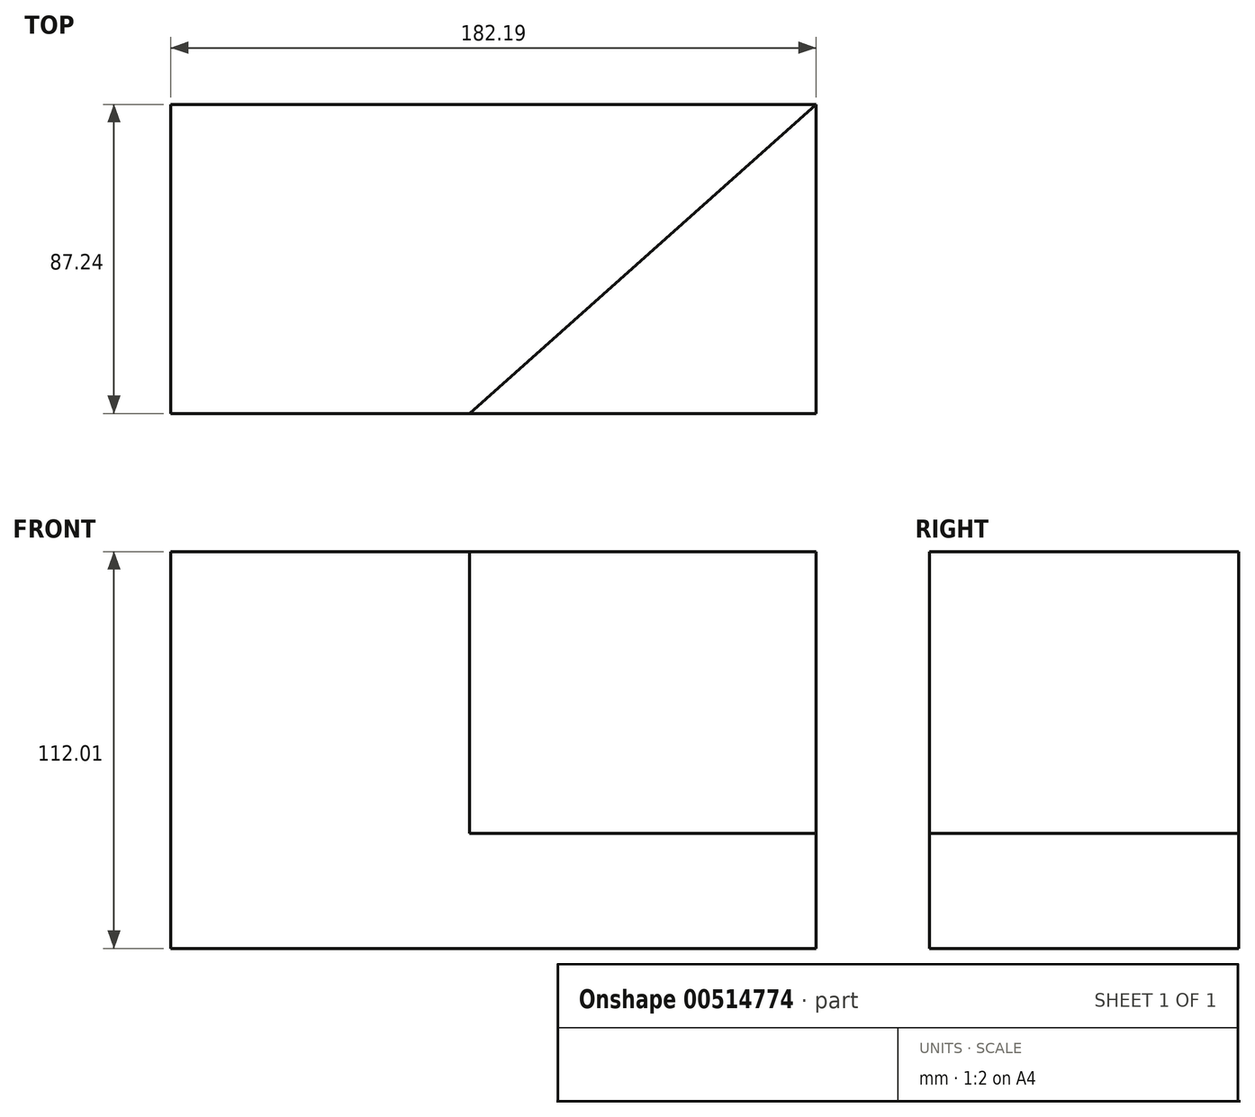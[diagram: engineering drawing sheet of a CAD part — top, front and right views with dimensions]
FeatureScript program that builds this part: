
annotation { "Feature Type Name" : "Feature", "Feature Type Description" : "" }
export const myFeature = defineFeature(function(context is Context, id is Id, definition is map)
    precondition{}
    {
        {
            var Q0;
            Q0=qCreatedBy(makeId("Top.planeOp"),FACE);
            var sketch = newSketch(context, id + "F0", { "sketchPlane" : qUnion([Q0])});
            skLineSegment(sketch, "E0.bottom", {"start": v(-84.35, 53.02) * mm, "end": v(97.84, 53.02) * mm});
            skLineSegment(sketch, "E0.top", {"start": v(-84.35, -34.22) * mm, "end": v(97.84, -34.22) * mm});
            skLineSegment(sketch, "E0.left", {"start": v(-84.35, 53.02) * mm, "end": v(-84.35, -34.22) * mm});
            skLineSegment(sketch, "E0.right", {"start": v(97.84, 53.02) * mm, "end": v(97.84, -34.22) * mm});
            skLineSegment(sketch, "E1", {"start": v(0, -34.22) * mm, "end": v(97.84, 53.02) * mm});
            skSolve(sketch);
        }
        {
            var Q0;
            Q0=makeQuery(id+"F0.imprint","IMPRINT",FACE,{"disambiguationData":[TD([[makeQuery(id+"F0.imprint","IMPRINT",EDGE,{"derivedFrom":sQuery(id+"F0.wireOp",EDGE,"E0.bottom")}),-1.0]])]});
            extrude(context, id + "F1", {"entities" : qUnion([Q0]), "depth" : 112.01 * mm, "offsetDistance" : 25.4 * mm});
        }
        {
            var Q0;
            Q0 = qSketchRegion(id + "F0", true);
            extrude(context, id + "F2", {"entities" : qUnion([Q0]), "operationType" : NewBodyOperationType.ADD, "depth" : 32.5 * mm, "offsetDistance" : 25.4 * mm});
        }
    });
